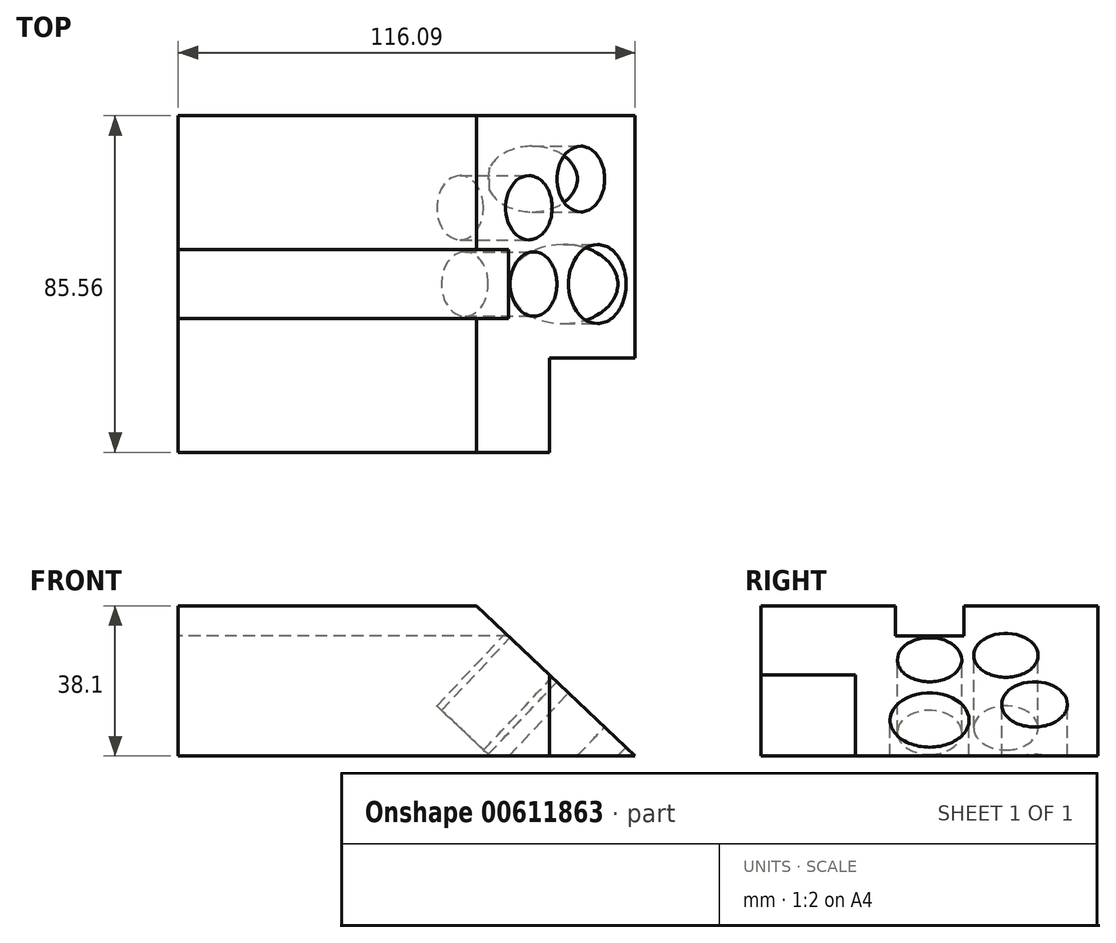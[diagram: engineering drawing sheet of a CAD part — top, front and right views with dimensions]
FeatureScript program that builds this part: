
annotation { "Feature Type Name" : "Feature", "Feature Type Description" : "" }
export const myFeature = defineFeature(function(context is Context, id is Id, definition is map)
    precondition{}
    {
        {
            var Q0;
            Q0=qCreatedBy(makeId("Top.planeOp"),FACE);
            var sketch = newSketch(context, id + "F0", { "sketchPlane" : qUnion([Q0])});
            skLineSegment(sketch, "E0.bottom", {"start": v(58.48, 30.08) * mm, "end": v(-58.48, 30.08) * mm});
            skLineSegment(sketch, "E0.top", {"start": v(58.48, -30.08) * mm, "end": v(-58.48, -30.08) * mm});
            skLineSegment(sketch, "E0.left", {"start": v(58.48, 30.08) * mm, "end": v(58.48, -30.08) * mm});
            skLineSegment(sketch, "E0.right", {"start": v(-58.48, 30.08) * mm, "end": v(-58.48, -30.08) * mm});
            skPoint(sketch, "E0.middle", {"position": v(0, 0) * mm});
            skSolve(sketch);
        }
        {
            var Q0;
            Q0=makeQuery(id+"F0.imprint","IMPRINT",FACE,{"disambiguationData":[TD([[makeQuery(id+"F0.imprint","IMPRINT",EDGE,{"derivedFrom":sQuery(id+"F0.wireOp",EDGE,"E0.bottom")}),1.0]])]});
            extrude(context, id + "F1", {"entities" : qUnion([Q0]), "depth" : 38.1 * mm, "offsetDistance" : 25.4 * mm});
        }
        {
            var Q0;
            Q0=qCreatedBy(makeId("Front.planeOp"),FACE);
            var sketch = newSketch(context, id + "F2", { "sketchPlane" : qUnion([Q0])});
            skLineSegment(sketch, "E1", {"start": v(14.81, 40.46) * mm, "end": v(65.2, -7.18) * mm});
            skLineSegment(sketch, "E2", {"start": v(65.2, -7.18) * mm, "end": v(65.2, 43.82) * mm});
            skLineSegment(sketch, "E3", {"start": v(65.2, 43.82) * mm, "end": v(13.28, 43.82) * mm});
            skLineSegment(sketch, "E4", {"start": v(13.28, 43.82) * mm, "end": v(14.81, 40.46) * mm});
            skSolve(sketch);
        }
        {
            var Q0;
            Q0=makeQuery(id+"F2.imprint","IMPRINT",FACE,{"disambiguationData":[TD([[makeQuery(id+"F2.imprint","IMPRINT",EDGE,{"derivedFrom":sQuery(id+"F2.wireOp",EDGE,"E1")}),1.0]])]});
            extrude(context, id + "F3", {"entities" : qUnion([Q0]), "operationType" : NewBodyOperationType.REMOVE, "endBound" : BoundingType.SYMMETRIC, "oppositeDirection" : true, "depth" : 63.5 * mm, "offsetDistance" : 25.4 * mm});
        }
        {
            var Q0;
            Q0=makeQuery(id+"F1.opExtrude","CAP_FACE",FACE,{"disambiguationData":[OSD([sQuery(id+"F0.wireOp",EDGE,"E0.bottom"),sQuery(id+"F0.wireOp",EDGE,"E0.top"),sQuery(id+"F0.wireOp",EDGE,"E0.left"),sQuery(id+"F0.wireOp",EDGE,"E0.right")])],"isStart":false});
            var sketch = newSketch(context, id + "F4", { "sketchPlane" : qUnion([Q0])});
            skLineSegment(sketch, "E5.bottom", {"start": v(26.11, -8.7) * mm, "end": v(-86.27, -8.7) * mm});
            skLineSegment(sketch, "E5.top", {"start": v(26.11, 8.7) * mm, "end": v(-86.27, 8.7) * mm});
            skLineSegment(sketch, "E5.left", {"start": v(26.11, -8.7) * mm, "end": v(26.11, 8.7) * mm});
            skLineSegment(sketch, "E5.right", {"start": v(-86.27, -8.7) * mm, "end": v(-86.27, 8.7) * mm});
            skPoint(sketch, "E5.middle", {"position": v(-30.08, 0) * mm});
            skSolve(sketch);
        }
        {
            var Q0;
            {var subQ0=sQuery(id+"F4.wireOp",EDGE,"E5.left");Q0=makeQuery(id+"F4.imprint","IMPRINT",FACE,{"disambiguationData":[TD([[makeQuery(id+"F4.imprint","IMPRINT",EDGE,{"derivedFrom":subQ0}),1.0]])]});}
            var Q1;
            {var subQ0=sQuery(id+"F4.wireOp",EDGE,"E5.bottom");var subQ1=sQuery(id+"F0.wireOp",EDGE,"E0.right");var subQ4=makeQuery(id+"F1.opExtrude","CAP_EDGE",EDGE,{"disambiguationData":[OSD([subQ1])],"isStart":false});var subQ5=makeQuery(id+"F4.imprint","INTERSECT",VERTEX,{"derivedFrom":[subQ4,subQ0]});Q1=makeQuery(id+"F4.imprint","IMPRINT",FACE,{"disambiguationData":[TD([[makeQuery(id+"F4.imprint","IMPRINT",EDGE,{"disambiguationData":[TD([[subQ5,1.0]])],"derivedFrom":subQ4}),1.0]])]});}
            extrude(context, id + "F5", {"entities" : qUnion([Q0, Q1]), "operationType" : NewBodyOperationType.REMOVE, "oppositeDirection" : true, "depth" : 7.62 * mm, "offsetDistance" : 25.4 * mm});
        }
        {
            var Q0;
            Q0=makeQuery(id+"F1.opExtrude","SWEPT_FACE",FACE,{"disambiguationData":[OSD([sQuery(id+"F0.wireOp",EDGE,"E0.top")])]});
            extrude(context, id + "F6", {"entities" : qUnion([Q0]), "operationType" : NewBodyOperationType.ADD, "depth" : 12.7 * mm, "offsetDistance" : 25.4 * mm});
        }
        {
            var Q0;
            Q0=makeQuery(id+"F1.opExtrude","SWEPT_FACE",FACE,{"disambiguationData":[OSD([sQuery(id+"F0.wireOp",EDGE,"E0.bottom")])]});
            extrude(context, id + "F7", {"entities" : qUnion([Q0]), "operationType" : NewBodyOperationType.ADD, "depth" : 12.7 * mm, "offsetDistance" : 25.4 * mm});
        }
        {
            var Q0;
            Q0=qCreatedBy(makeId("Top.planeOp"),FACE);
            var sketch = newSketch(context, id + "F8", { "sketchPlane" : qUnion([Q0])});
            skLineSegment(sketch, "E6.bottom", {"start": v(35.88, -46.57) * mm, "end": v(61.84, -46.57) * mm});
            skLineSegment(sketch, "E6.top", {"start": v(35.88, -18.78) * mm, "end": v(61.84, -18.78) * mm});
            skLineSegment(sketch, "E6.left", {"start": v(35.88, -46.57) * mm, "end": v(35.88, -18.78) * mm});
            skLineSegment(sketch, "E6.right", {"start": v(61.84, -46.57) * mm, "end": v(61.84, -18.78) * mm});
            skSolve(sketch);
        }
        {
            var Q0;
            Q0=makeQuery(id+"F8.imprint","IMPRINT",FACE,{"disambiguationData":[TD([[makeQuery(id+"F8.imprint","IMPRINT",EDGE,{"derivedFrom":sQuery(id+"F8.wireOp",EDGE,"E6.bottom")}),1.0]])]});
            extrude(context, id + "F9", {"entities" : qUnion([Q0]), "operationType" : NewBodyOperationType.REMOVE, "depth" : 25.4 * mm, "offsetDistance" : 25.4 * mm});
        }
        {
            var Q0;
            {var subQ0=sQuery(id+"F2.wireOp",EDGE,"E1");Q0=makeQuery(id+"F7.boolean.opBoolean","MERGE",FACE,{"derivedFrom":[makeQuery(id+"F6.boolean.opBoolean","MERGE",FACE,{"derivedFrom":[makeQuery(id+"F3.boolean.opBoolean","COPY",FACE,{"derivedFrom":makeQuery(id+"F3.opExtrude","SWEPT_FACE",FACE,{"disambiguationData":[OSD([subQ0])]})}),makeQuery(id+"F6.opExtrude","SWEPT_FACE",FACE,{"disambiguationData":[OSD([sQuery(id+"F0.wireOp",EDGE,"E0.top"),subQ0])]})]}),makeQuery(id+"F7.opExtrude","SWEPT_FACE",FACE,{"disambiguationData":[OSD([sQuery(id+"F0.wireOp",EDGE,"E0.bottom"),subQ0])]})]});}
            var sketch = newSketch(context, id + "F10", { "sketchPlane" : qUnion([Q0])});
            skCircle(sketch, "E7", {"center": v(13.64, 0) * mm, "radius": 10.84 * mm});
            skCircle(sketch, "E8", {"center": v(31.02, 0) * mm, "radius": 8.7 * mm});
            skCircle(sketch, "E9", {"center": v(4.68, 19.39) * mm, "radius": 8.15 * mm});
            skCircle(sketch, "E10", {"center": v(24.86, 20) * mm, "radius": 9 * mm});
            skSolve(sketch);
        }
        {
            var Q0;
            Q0=makeQuery(id+"F10.imprint","IMPRINT",FACE,{"disambiguationData":[TD([[makeQuery(id+"F10.imprint","IMPRINT",EDGE,{"derivedFrom":sQuery(id+"F10.wireOp",EDGE,"E9")}),1.0]])]});
            extrude(context, id + "F11", {"entities" : qUnion([Q0]), "operationType" : NewBodyOperationType.REMOVE, "oppositeDirection" : true, "depth" : 25.4 * mm, "offsetDistance" : 25.4 * mm});
        }
        {
            var Q0;
            {var subQ0=sQuery(id+"F2.wireOp",EDGE,"E1");Q0=makeQuery(id+"F7.boolean.opBoolean","MERGE",FACE,{"derivedFrom":[makeQuery(id+"F6.boolean.opBoolean","MERGE",FACE,{"derivedFrom":[makeQuery(id+"F3.boolean.opBoolean","COPY",FACE,{"derivedFrom":makeQuery(id+"F3.opExtrude","SWEPT_FACE",FACE,{"disambiguationData":[OSD([subQ0])]})}),makeQuery(id+"F6.opExtrude","SWEPT_FACE",FACE,{"disambiguationData":[OSD([sQuery(id+"F0.wireOp",EDGE,"E0.top"),subQ0])]})]}),makeQuery(id+"F7.opExtrude","SWEPT_FACE",FACE,{"disambiguationData":[OSD([sQuery(id+"F0.wireOp",EDGE,"E0.bottom"),subQ0])]})]});}
            var sketch = newSketch(context, id + "F12", { "sketchPlane" : qUnion([Q0])});
            skCircle(sketch, "E11", {"center": v(6.31, 0) * mm, "radius": 8.17 * mm});
            skSolve(sketch);
        }
        {
            var Q0;
            Q0=makeQuery(id+"F12.imprint","IMPRINT",FACE,{"disambiguationData":[TD([[makeQuery(id+"F12.imprint","IMPRINT",EDGE,{"derivedFrom":sQuery(id+"F12.wireOp",EDGE,"E11")}),1.0]])]});
            extrude(context, id + "F13", {"entities" : qUnion([Q0]), "operationType" : NewBodyOperationType.REMOVE, "oppositeDirection" : true, "depth" : 25.4 * mm, "offsetDistance" : 25.4 * mm});
        }
        {
            var Q0;
            {var subQ0=sQuery(id+"F2.wireOp",EDGE,"E1");Q0=makeQuery(id+"F7.boolean.opBoolean","MERGE",FACE,{"derivedFrom":[makeQuery(id+"F6.boolean.opBoolean","MERGE",FACE,{"derivedFrom":[makeQuery(id+"F3.boolean.opBoolean","COPY",FACE,{"derivedFrom":makeQuery(id+"F3.opExtrude","SWEPT_FACE",FACE,{"disambiguationData":[OSD([subQ0])]})}),makeQuery(id+"F6.opExtrude","SWEPT_FACE",FACE,{"disambiguationData":[OSD([sQuery(id+"F0.wireOp",EDGE,"E0.top"),subQ0])]})]}),makeQuery(id+"F7.opExtrude","SWEPT_FACE",FACE,{"disambiguationData":[OSD([sQuery(id+"F0.wireOp",EDGE,"E0.bottom"),subQ0])]})]});}
            var sketch = newSketch(context, id + "F14", { "sketchPlane" : qUnion([Q0])});
            skCircle(sketch, "E12", {"center": v(28.6, 0) * mm, "radius": 10.05 * mm});
            skSolve(sketch);
        }
        {
            var Q0;
            Q0=makeQuery(id+"F14.imprint","IMPRINT",FACE,{"disambiguationData":[TD([[makeQuery(id+"F14.imprint","IMPRINT",EDGE,{"derivedFrom":sQuery(id+"F14.wireOp",EDGE,"E12")}),1.0]])]});
            extrude(context, id + "F15", {"entities" : qUnion([Q0]), "operationType" : NewBodyOperationType.REMOVE, "oppositeDirection" : true, "depth" : 25.4 * mm, "offsetDistance" : 25.4 * mm});
        }
        {
            var Q0;
            {var subQ0=sQuery(id+"F2.wireOp",EDGE,"E1");Q0=makeQuery(id+"F7.boolean.opBoolean","MERGE",FACE,{"derivedFrom":[makeQuery(id+"F6.boolean.opBoolean","MERGE",FACE,{"derivedFrom":[makeQuery(id+"F3.boolean.opBoolean","COPY",FACE,{"derivedFrom":makeQuery(id+"F3.opExtrude","SWEPT_FACE",FACE,{"disambiguationData":[OSD([subQ0])]})}),makeQuery(id+"F6.opExtrude","SWEPT_FACE",FACE,{"disambiguationData":[OSD([sQuery(id+"F0.wireOp",EDGE,"E0.top"),subQ0])]})]}),makeQuery(id+"F7.opExtrude","SWEPT_FACE",FACE,{"disambiguationData":[OSD([sQuery(id+"F0.wireOp",EDGE,"E0.bottom"),subQ0])]})]});}
            var sketch = newSketch(context, id + "F16", { "sketchPlane" : qUnion([Q0])});
            skCircle(sketch, "E13", {"center": v(22.83, 26.67) * mm, "radius": 8.35 * mm});
            skSolve(sketch);
        }
        {
            var Q0;
            Q0=makeQuery(id+"F16.imprint","IMPRINT",FACE,{"disambiguationData":[TD([[makeQuery(id+"F16.imprint","IMPRINT",EDGE,{"derivedFrom":sQuery(id+"F16.wireOp",EDGE,"E13")}),1.0]])]});
            extrude(context, id + "F17", {"entities" : qUnion([Q0]), "operationType" : NewBodyOperationType.REMOVE, "oppositeDirection" : true, "depth" : 25.4 * mm, "offsetDistance" : 25.4 * mm});
        }
    });
